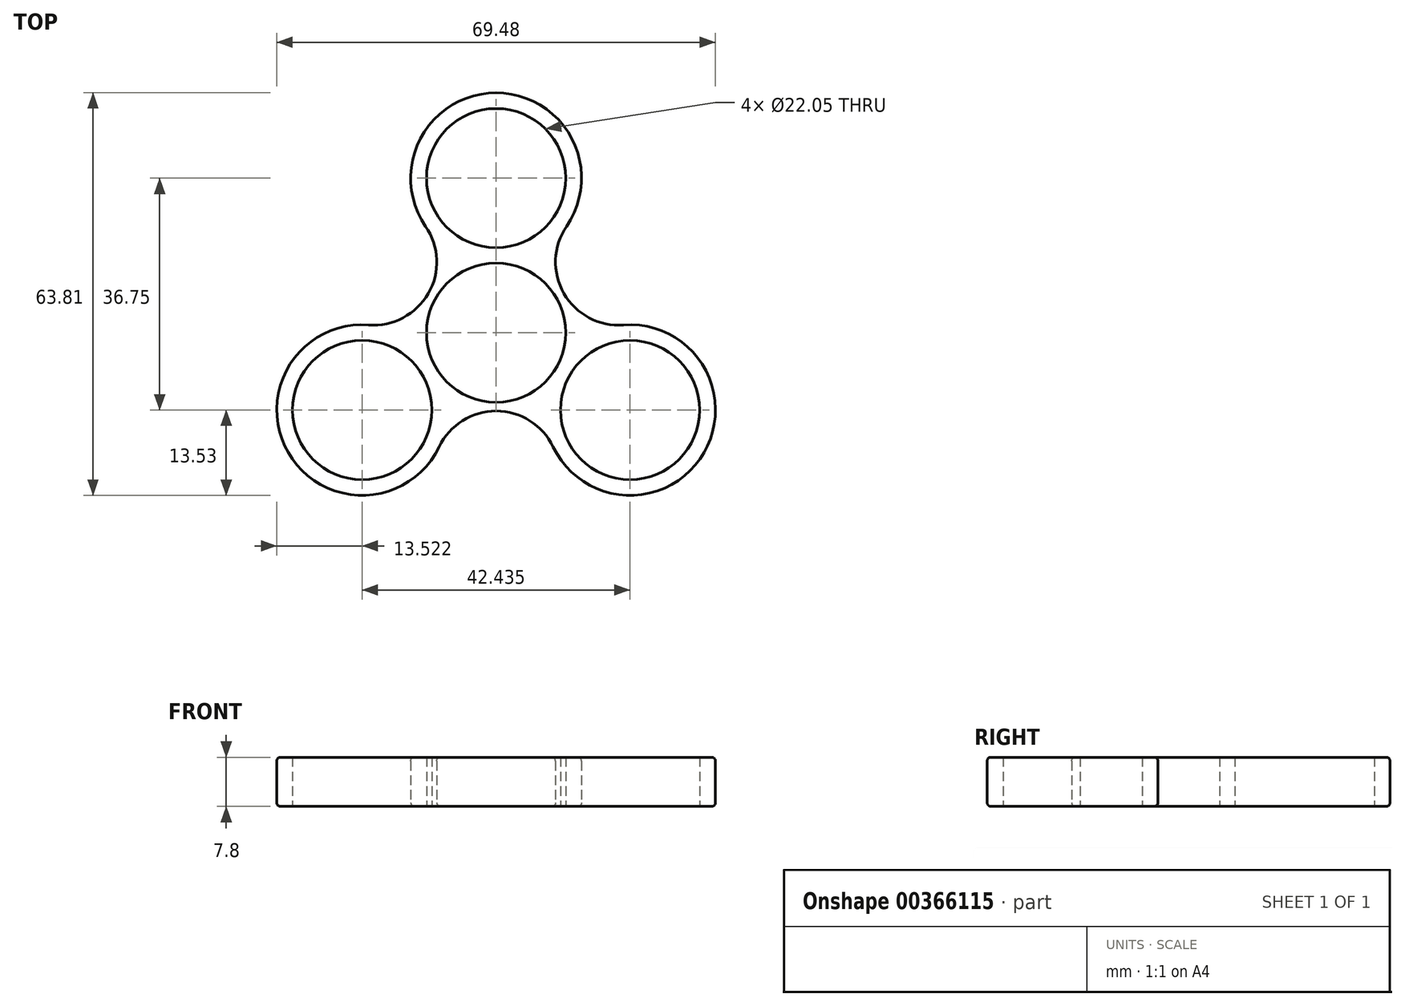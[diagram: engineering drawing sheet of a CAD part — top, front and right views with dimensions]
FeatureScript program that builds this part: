
annotation { "Feature Type Name" : "Feature", "Feature Type Description" : "" }
export const myFeature = defineFeature(function(context is Context, id is Id, definition is map)
    precondition{}
    {
        {
            var Q0;
            Q0=qCreatedBy(makeId("Top.planeOp"),FACE);
            var sketch = newSketch(context, id + "F0", { "sketchPlane" : qUnion([Q0])});
            skCircle(sketch, "E0", {"center": v(0, 0) * mm, "radius": 11.03 * mm});
            skCircle(sketch, "E1", {"center": v(0, 24.5) * mm, "radius": 11.03 * mm});
            skArc(sketch, "E2.0", {"start": v(11.16, 16.86) * mm, "mid": v(0, 38.03) * mm, "end": v(-11.16, 16.86) * mm});
            skArc(sketch, "E3.1.0", {"start": v(-20.18, 1.23) * mm, "mid": v(-32.93, -19.01) * mm, "end": v(-9.02, -18.1) * mm});
            skCircle(sketch, "E3.1.1", {"center": v(-21.22, -12.25) * mm, "radius": 11.03 * mm});
            skArc(sketch, "E3.2.0", {"start": v(9.02, -18.1) * mm, "mid": v(32.93, -19.01) * mm, "end": v(20.18, 1.23) * mm});
            skCircle(sketch, "E3.2.1", {"center": v(21.22, -12.25) * mm, "radius": 11.03 * mm});
            skArc(sketch, "E4", {"start": v(11.16, 16.86) * mm, "mid": v(10.75, 6.2) * mm, "end": v(20.18, 1.23) * mm});
            skArc(sketch, "E5.1.0", {"start": v(-20.18, 1.23) * mm, "mid": v(-10.75, 6.2) * mm, "end": v(-11.16, 16.86) * mm});
            skArc(sketch, "E5.2.0", {"start": v(9.02, -18.1) * mm, "mid": v(0, -12.41) * mm, "end": v(-9.02, -18.1) * mm});
            skSolve(sketch);
        }
        {
            var Q0;
            Q0 = qSketchRegion(id + "F0", true);
            extrude(context, id + "F1", {"entities" : qUnion([Q0]), "depth" : 7.8 * mm, "offsetDistance" : 25 * mm});
        }
        {
            var Q0;
            Q0=makeQuery(id+"F1.opExtrude","CAP_EDGE",EDGE,{"disambiguationData":[OSD([sQuery(id+"F0.wireOp",EDGE,"E3.1.0")])],"isStart":true});
            var Q1;
            Q1=makeQuery(id+"F1.opExtrude","CAP_EDGE",EDGE,{"disambiguationData":[OSD([sQuery(id+"F0.wireOp",EDGE,"E5.2.0")])],"isStart":true});
            var Q2;
            Q2=makeQuery(id+"F1.opExtrude","CAP_EDGE",EDGE,{"disambiguationData":[OSD([sQuery(id+"F0.wireOp",EDGE,"E3.1.0")])],"isStart":false});
            fillet(context, id + "F2", {"entities" : qUnion([Q0, Q1, Q2]), "radius" : .6 * mm, "tangentPropagation" : true, "allowEdgeOverflow" : false});
        }
    });
